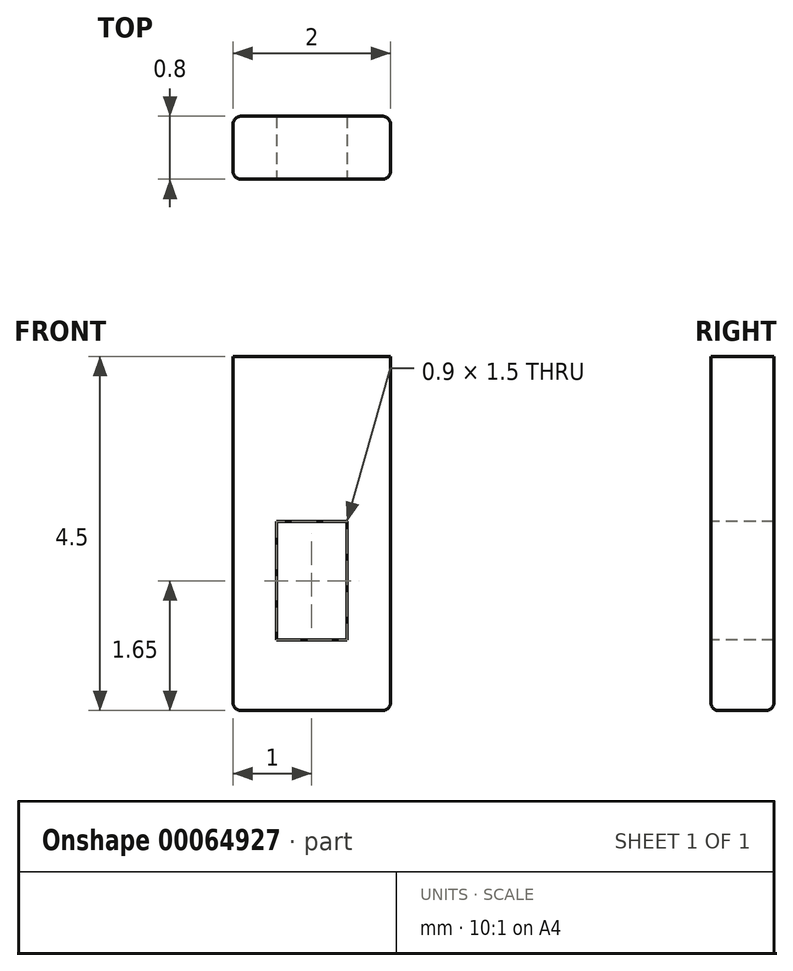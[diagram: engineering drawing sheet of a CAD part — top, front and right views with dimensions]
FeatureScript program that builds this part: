
annotation { "Feature Type Name" : "Feature", "Feature Type Description" : "" }
export const myFeature = defineFeature(function(context is Context, id is Id, definition is map)
    precondition{}
    {
        {
            var Q0;
            Q0=qCreatedBy(makeId("Front.planeOp"),FACE);
            var sketch = newSketch(context, id + "F0", { "sketchPlane" : qUnion([Q0])});
            skLineSegment(sketch, "E0.bottom", {"start": v(0, 0) * mm, "end": v(2, 0) * mm});
            skLineSegment(sketch, "E0.top", {"start": v(0, 4.5) * mm, "end": v(2, 4.5) * mm});
            skLineSegment(sketch, "E0.left", {"start": v(0, 0) * mm, "end": v(0, 4.5) * mm});
            skLineSegment(sketch, "E0.right", {"start": v(2, 0) * mm, "end": v(2, 4.5) * mm});
            skSolve(sketch);
        }
        {
            var Q0;
            Q0=makeQuery(id+"F0.imprint","IMPRINT",FACE,{"disambiguationData":[TD([[makeQuery(id+"F0.imprint","IMPRINT",EDGE,{"derivedFrom":sQuery(id+"F0.wireOp",EDGE,"E0.bottom")}),1.0]])]});
            extrude(context, id + "F1", {"entities" : qUnion([Q0]), "depth" : .8 * mm});
        }
        {
            var Q0;
            Q0=makeQuery(id+"F1.opExtrude","CAP_FACE",FACE,{"disambiguationData":[OSD([sQuery(id+"F0.wireOp",EDGE,"E0.bottom"),sQuery(id+"F0.wireOp",EDGE,"E0.top"),sQuery(id+"F0.wireOp",EDGE,"E0.left"),sQuery(id+"F0.wireOp",EDGE,"E0.right")])],"isStart":false});
            var sketch = newSketch(context, id + "F2", { "sketchPlane" : qUnion([Q0])});
            skLineSegment(sketch, "E1", {"start": v(1, 0.9) * mm, "end": v(1.45, 0.9) * mm});
            skPoint(sketch, "E1.startSnap0", {"position": v(1, 0) * mm});
            skLineSegment(sketch, "E2", {"start": v(1.45, 0.9) * mm, "end": v(1.45, 2.4) * mm});
            skLineSegment(sketch, "E3", {"start": v(1.45, 2.4) * mm, "end": v(0.55, 2.4) * mm});
            skLineSegment(sketch, "E4", {"start": v(0.55, 2.4) * mm, "end": v(0.55, 0.9) * mm});
            skLineSegment(sketch, "E5", {"start": v(0.55, 0.9) * mm, "end": v(1, 0.9) * mm});
            skSolve(sketch);
        }
        {
            var Q0;
            Q0=makeQuery(id+"F2.imprint","IMPRINT",FACE,{"disambiguationData":[TD([[makeQuery(id+"F2.imprint","IMPRINT",EDGE,{"derivedFrom":sQuery(id+"F2.wireOp",EDGE,"E1")}),1.0]])]});
            extrude(context, id + "F3", {"entities" : qUnion([Q0]), "operationType" : NewBodyOperationType.REMOVE, "oppositeDirection" : true, "depth" : 25.4 * mm});
        }
        {
            var Q0;
            Q0=makeQuery(id+"F1.opExtrude","CAP_EDGE",EDGE,{"disambiguationData":[OSD([sQuery(id+"F0.wireOp",EDGE,"E0.right")])],"isStart":false});
            var Q1;
            Q1=makeQuery(id+"F1.opExtrude","CAP_EDGE",EDGE,{"disambiguationData":[OSD([sQuery(id+"F0.wireOp",EDGE,"E0.bottom")])],"isStart":false});
            var Q2;
            Q2=makeQuery(id+"F1.opExtrude","CAP_EDGE",EDGE,{"disambiguationData":[OSD([sQuery(id+"F0.wireOp",EDGE,"E0.left")])],"isStart":false});
            var Q3;
            Q3=makeQuery(id+"F1.opExtrude","CAP_EDGE",EDGE,{"disambiguationData":[OSD([sQuery(id+"F0.wireOp",EDGE,"E0.right")])],"isStart":true});
            var Q4;
            Q4=makeQuery(id+"F1.opExtrude","CAP_EDGE",EDGE,{"disambiguationData":[OSD([sQuery(id+"F0.wireOp",EDGE,"E0.bottom")])],"isStart":true});
            var Q5;
            Q5=makeQuery(id+"F1.opExtrude","CAP_EDGE",EDGE,{"disambiguationData":[OSD([sQuery(id+"F0.wireOp",EDGE,"E0.left")])],"isStart":true});
            fillet(context, id + "F4", {"entities" : qUnion([Q0, Q1, Q2, Q3, Q4, Q5]), "radius" : .1 * mm, "tangentPropagation" : true, "allowEdgeOverflow" : false});
        }
        {
            var Q0;
            Q0=makeQuery(id+"F1.opExtrude","SWEPT_EDGE",EDGE,{"disambiguationData":[OSD([sQuery(id+"F0.wireOp",EDGE,"E0.bottom"),sQuery(id+"F0.wireOp",EDGE,"E0.left")])]});
            var Q1;
            Q1=makeQuery(id+"F1.opExtrude","SWEPT_EDGE",EDGE,{"disambiguationData":[OSD([sQuery(id+"F0.wireOp",EDGE,"E0.bottom"),sQuery(id+"F0.wireOp",EDGE,"E0.right")])]});
            fillet(context, id + "F5", {"entities" : qUnion([Q0, Q1]), "radius" : .1 * mm, "tangentPropagation" : true, "allowEdgeOverflow" : false});
        }
    });
